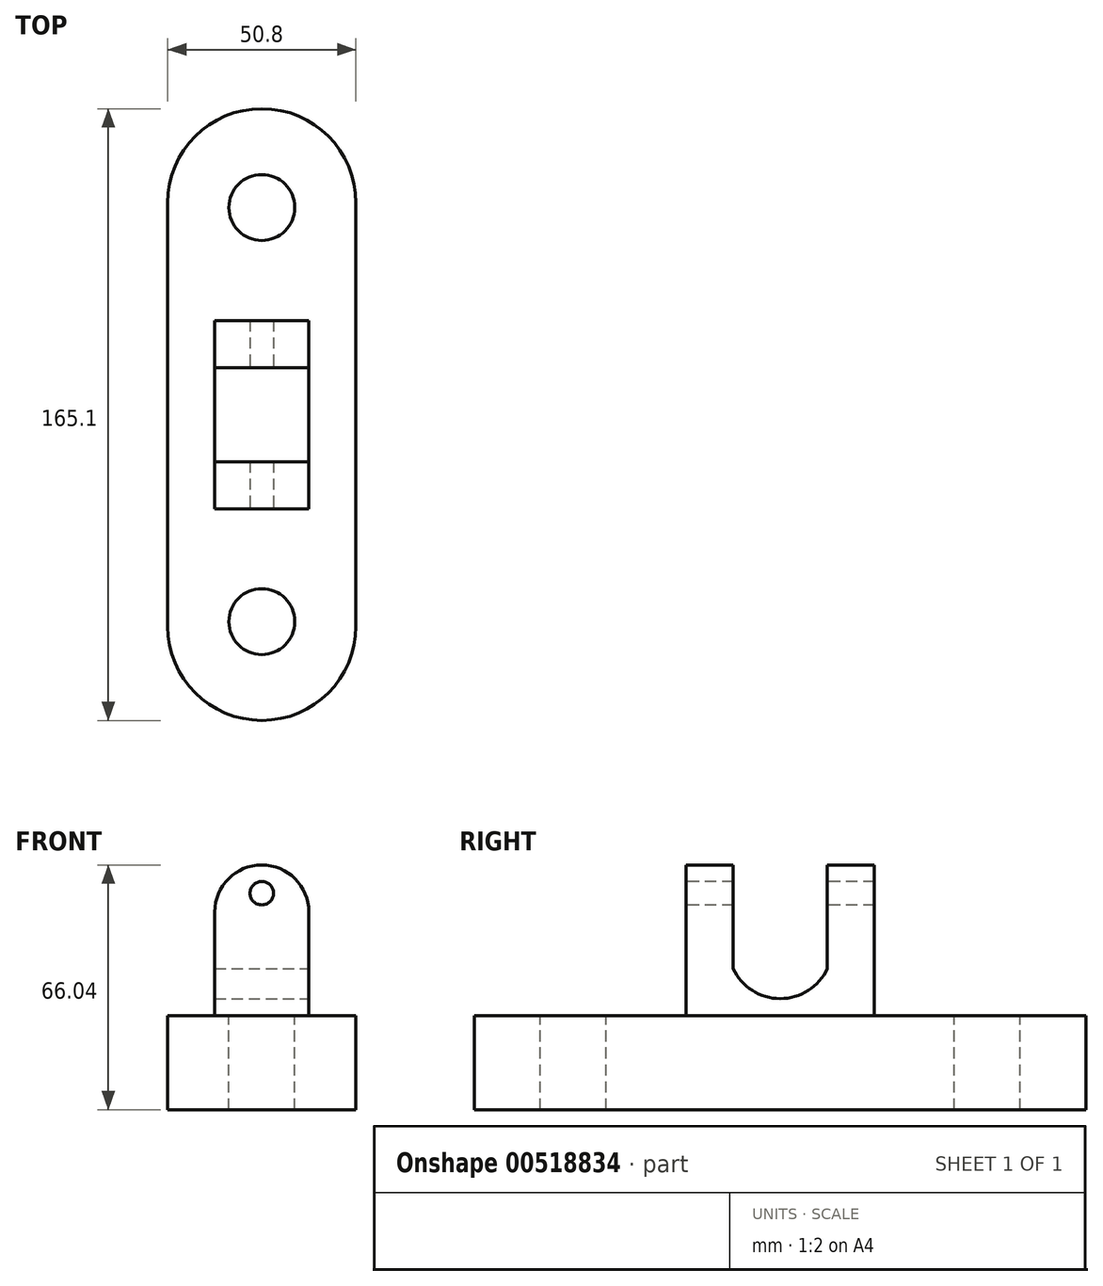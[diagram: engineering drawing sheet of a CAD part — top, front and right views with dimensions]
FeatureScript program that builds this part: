
annotation { "Feature Type Name" : "Feature", "Feature Type Description" : "" }
export const myFeature = defineFeature(function(context is Context, id is Id, definition is map)
    precondition{}
    {
        {
            var Q0;
            Q0=qCreatedBy(makeId("Top.planeOp"),FACE);
            var sketch = newSketch(context, id + "F0", { "sketchPlane" : qUnion([Q0])});
            skLineSegment(sketch, "E0.bottom", {"start": v(25.4, 57.15) * mm, "end": v(-25.4, 57.15) * mm});
            skLineSegment(sketch, "E0.top", {"start": v(25.4, -57.15) * mm, "end": v(-25.4, -57.15) * mm});
            skLineSegment(sketch, "E0.left", {"start": v(25.4, 57.15) * mm, "end": v(25.4, -57.15) * mm});
            skLineSegment(sketch, "E0.right", {"start": v(-25.4, 57.15) * mm, "end": v(-25.4, -57.15) * mm});
            skPoint(sketch, "E0.middle", {"position": v(0, 0) * mm});
            skArc(sketch, "E1", {"start": v(25.4, 57.15) * mm, "mid": v(0, 82.55) * mm, "end": v(-25.4, 57.15) * mm});
            skArc(sketch, "E2", {"start": v(-25.4, -57.15) * mm, "mid": v(0, -82.55) * mm, "end": v(25.4, -57.15) * mm});
            skSolve(sketch);
        }
        {
            var Q0;
            Q0=makeQuery(id+"F0.imprint","IMPRINT",FACE,{"disambiguationData":[TD([[makeQuery(id+"F0.imprint","IMPRINT",EDGE,{"derivedFrom":sQuery(id+"F0.wireOp",EDGE,"E0.bottom")}),-1.0]])]});
            var Q1;
            Q1=makeQuery(id+"F0.imprint","IMPRINT",FACE,{"disambiguationData":[TD([[makeQuery(id+"F0.imprint","IMPRINT",EDGE,{"derivedFrom":sQuery(id+"F0.wireOp",EDGE,"E0.bottom")}),1.0]])]});
            var Q2;
            Q2=makeQuery(id+"F0.imprint","IMPRINT",FACE,{"disambiguationData":[TD([[makeQuery(id+"F0.imprint","IMPRINT",EDGE,{"derivedFrom":sQuery(id+"F0.wireOp",EDGE,"E0.top")}),1.0]])]});
            extrude(context, id + "F1", {"entities" : qUnion([Q0, Q1, Q2]), "endBound" : BoundingType.SYMMETRIC, "depth" : 25.4 * mm, "offsetDistance" : 25.4 * mm});
        }
        {
            var Q0;
            Q0=makeQuery(id+"F1.opExtrude","CAP_FACE",FACE,{"disambiguationData":[OSD([sQuery(id+"F0.wireOp",EDGE,"E0.left"),sQuery(id+"F0.wireOp",EDGE,"E0.right"),sQuery(id+"F0.wireOp",EDGE,"E1"),sQuery(id+"F0.wireOp",EDGE,"E2")])],"isStart":false});
            var sketch = newSketch(context, id + "F2", { "sketchPlane" : qUnion([Q0])});
            skCircle(sketch, "E3", {"center": v(0, 55.88) * mm, "radius": 8.9 * mm});
            skCircle(sketch, "E4", {"center": v(0, -55.88) * mm, "radius": 8.9 * mm});
            skSolve(sketch);
        }
        {
            var Q0;
            Q0=makeQuery(id+"F2.imprint","IMPRINT",FACE,{"disambiguationData":[TD([[makeQuery(id+"F2.imprint","IMPRINT",EDGE,{"derivedFrom":sQuery(id+"F2.wireOp",EDGE,"E3")}),1.0]])]});
            var Q1;
            Q1=makeQuery(id+"F2.imprint","IMPRINT",FACE,{"disambiguationData":[TD([[makeQuery(id+"F2.imprint","IMPRINT",EDGE,{"derivedFrom":sQuery(id+"F2.wireOp",EDGE,"E4")}),1.0]])]});
            extrude(context, id + "F3", {"entities" : qUnion([Q0, Q1]), "operationType" : NewBodyOperationType.REMOVE, "oppositeDirection" : true, "depth" : 63.5 * mm, "offsetDistance" : 25.4 * mm});
        }
        {
            var Q0;
            Q0=makeQuery(id+"F1.opExtrude","CAP_FACE",FACE,{"disambiguationData":[OSD([sQuery(id+"F0.wireOp",EDGE,"E0.left"),sQuery(id+"F0.wireOp",EDGE,"E0.right"),sQuery(id+"F0.wireOp",EDGE,"E1"),sQuery(id+"F0.wireOp",EDGE,"E2")])],"isStart":false});
            var sketch = newSketch(context, id + "F4", { "sketchPlane" : qUnion([Q0])});
            skLineSegment(sketch, "E5.bottom", {"start": v(12.7, 25.4) * mm, "end": v(-12.7, 25.4) * mm});
            skLineSegment(sketch, "E5.top", {"start": v(12.7, -25.4) * mm, "end": v(-12.7, -25.4) * mm});
            skLineSegment(sketch, "E5.left", {"start": v(12.7, 25.4) * mm, "end": v(12.7, -25.4) * mm});
            skLineSegment(sketch, "E5.right", {"start": v(-12.7, 25.4) * mm, "end": v(-12.7, -25.4) * mm});
            skPoint(sketch, "E5.middle", {"position": v(0, 0) * mm});
            skSolve(sketch);
        }
        {
            var Q0;
            Q0 = qSketchRegion(id + "F4", true);
            extrude(context, id + "F5", {"entities" : qUnion([Q0]), "operationType" : NewBodyOperationType.ADD, "depth" : 27.94 * mm, "offsetDistance" : 25.4 * mm});
        }
        {
            var Q0;
            Q0=makeQuery(id+"F5.opExtrude","SWEPT_FACE",FACE,{"disambiguationData":[OSD([sQuery(id+"F4.wireOp",EDGE,"E5.top")])]});
            var sketch = newSketch(context, id + "F6", { "sketchPlane" : qUnion([Q0])});
            skArc(sketch, "E6", {"start": v(12.7, 40.64) * mm, "mid": v(0, 53.34) * mm, "end": v(-12.7, 40.64) * mm});
            skSolve(sketch);
        }
        {
            var Q0;
            Q0=makeQuery(id+"F5.opExtrude","SWEPT_FACE",FACE,{"disambiguationData":[OSD([sQuery(id+"F4.wireOp",EDGE,"E5.bottom")])]});
            var sketch = newSketch(context, id + "F7", { "sketchPlane" : qUnion([Q0])});
            skArc(sketch, "E7", {"start": v(12.7, 40.64) * mm, "mid": v(0, 53.34) * mm, "end": v(-12.7, 40.64) * mm});
            skSolve(sketch);
        }
        {
            var Q0;
            Q0=makeQuery(id+"F7.imprint","IMPRINT",FACE,{"disambiguationData":[TD([[makeQuery(id+"F7.imprint","IMPRINT",EDGE,{"derivedFrom":sQuery(id+"F7.wireOp",EDGE,"E7")}),1.0]])]});
            extrude(context, id + "F8", {"entities" : qUnion([Q0]), "operationType" : NewBodyOperationType.ADD, "oppositeDirection" : true, "depth" : 12.7 * mm, "offsetDistance" : 25.4 * mm});
        }
        {
            var Q0;
            Q0=makeQuery(id+"F6.imprint","IMPRINT",FACE,{"disambiguationData":[TD([[makeQuery(id+"F6.imprint","IMPRINT",EDGE,{"derivedFrom":sQuery(id+"F6.wireOp",EDGE,"E6")}),1.0]])]});
            extrude(context, id + "F9", {"entities" : qUnion([Q0]), "operationType" : NewBodyOperationType.ADD, "oppositeDirection" : true, "depth" : 12.7 * mm, "offsetDistance" : 25.4 * mm});
        }
        {
            var Q0;
            {var subQ0=sQuery(id+"F4.wireOp",EDGE,"E5.top");Q0=makeQuery(id+"F9.boolean.opBoolean","MERGE",FACE,{"derivedFrom":[makeQuery(id+"F5.opExtrude","SWEPT_FACE",FACE,{"disambiguationData":[OSD([subQ0])]}),makeQuery(id+"F9.opExtrude","CAP_FACE",FACE,{"disambiguationData":[OSD([subQ0,sQuery(id+"F6.wireOp",EDGE,"E6")])],"isStart":true})]});}
            var sketch = newSketch(context, id + "F10", { "sketchPlane" : qUnion([Q0])});
            skCircle(sketch, "E8", {"center": v(0, 45.72) * mm, "radius": 3.18 * mm});
            skSolve(sketch);
        }
        {
            var Q0;
            Q0=makeQuery(id+"F10.imprint","IMPRINT",FACE,{"disambiguationData":[TD([[makeQuery(id+"F10.imprint","IMPRINT",EDGE,{"derivedFrom":sQuery(id+"F10.wireOp",EDGE,"E8")}),1.0]])]});
            extrude(context, id + "F11", {"entities" : qUnion([Q0]), "operationType" : NewBodyOperationType.REMOVE, "oppositeDirection" : true, "depth" : 76.2 * mm, "offsetDistance" : 25.4 * mm});
        }
        {
            var Q0;
            Q0=makeQuery(id+"F5.opExtrude","SWEPT_FACE",FACE,{"disambiguationData":[OSD([sQuery(id+"F4.wireOp",EDGE,"E5.left")])]});
            var sketch = newSketch(context, id + "F12", { "sketchPlane" : qUnion([Q0])});
            skLineSegment(sketch, "E9.bottom", {"start": v(12.7, 40.64) * mm, "end": v(-12.7, 40.64) * mm});
            skLineSegment(sketch, "E9.top", {"start": v(12.7, 25.4) * mm, "end": v(-12.7, 25.4) * mm});
            skLineSegment(sketch, "E9.left", {"start": v(12.7, 40.64) * mm, "end": v(12.7, 25.4) * mm});
            skLineSegment(sketch, "E9.right", {"start": v(-12.7, 40.64) * mm, "end": v(-12.7, 25.4) * mm});
            skPoint(sketch, "E9.middle", {"position": v(0, 33.02) * mm});
            skArc(sketch, "E10", {"start": v(-12.7, 25.4) * mm, "mid": v(0, 17.25) * mm, "end": v(12.7, 25.4) * mm});
            skSolve(sketch);
        }
        {
            var Q0;
            Q0=makeQuery(id+"F12.imprint","IMPRINT",FACE,{"disambiguationData":[TD([[makeQuery(id+"F12.imprint","IMPRINT",EDGE,{"derivedFrom":sQuery(id+"F12.wireOp",EDGE,"E9.bottom")}),1.0]])]});
            var Q1;
            Q1=makeQuery(id+"F12.imprint","IMPRINT",FACE,{"disambiguationData":[TD([[makeQuery(id+"F12.imprint","IMPRINT",EDGE,{"derivedFrom":sQuery(id+"F12.wireOp",EDGE,"E9.top")}),1.0]])]});
            extrude(context, id + "F13", {"entities" : qUnion([Q0, Q1]), "operationType" : NewBodyOperationType.REMOVE, "oppositeDirection" : true, "depth" : 76.2 * mm, "offsetDistance" : 25.4 * mm});
        }
    });
